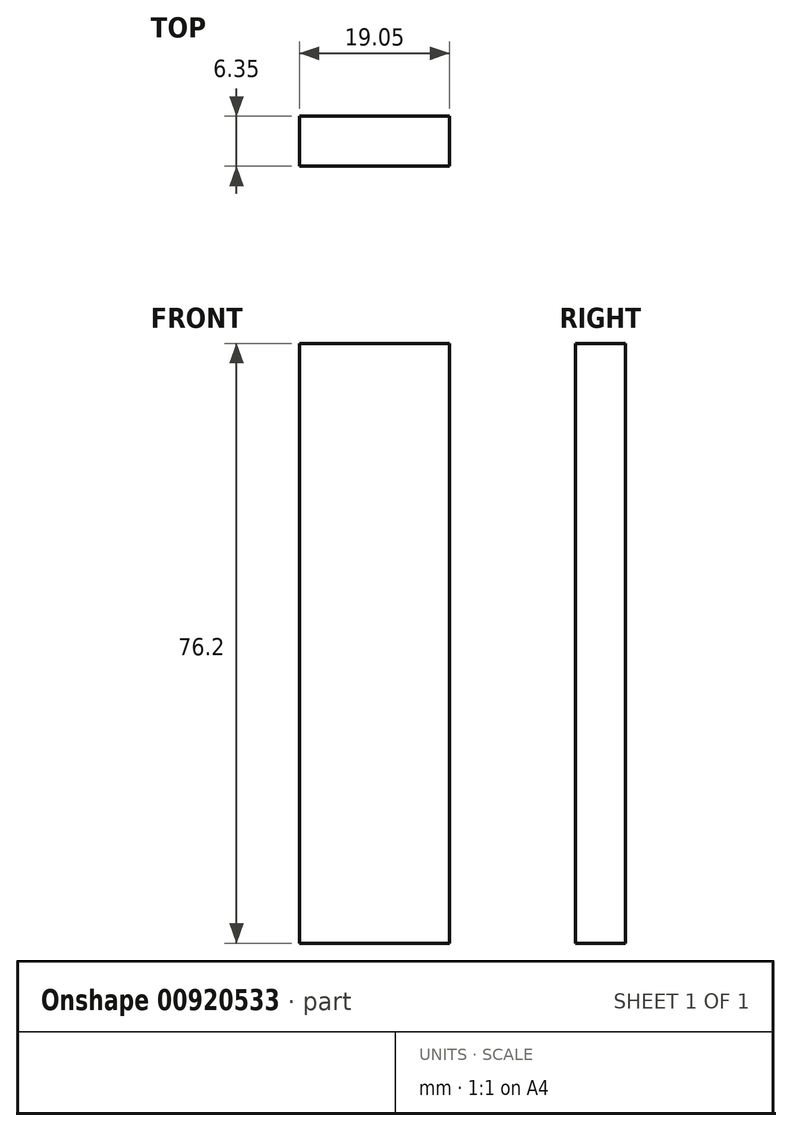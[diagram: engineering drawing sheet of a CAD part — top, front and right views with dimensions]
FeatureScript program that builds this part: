
annotation { "Feature Type Name" : "Feature", "Feature Type Description" : "" }
export const myFeature = defineFeature(function(context is Context, id is Id, definition is map)
    precondition{}
    {
        {
            var Q0;
            Q0=qCreatedBy(makeId("Front.planeOp"),FACE);
            var sketch = newSketch(context, id + "F0", { "sketchPlane" : qUnion([Q0])});
            skLineSegment(sketch, "E0.bottom", {"start": v(0, 38.1) * mm, "end": v(19.05, 38.1) * mm});
            skLineSegment(sketch, "E0.top", {"start": v(0, -38.1) * mm, "end": v(19.05, -38.1) * mm});
            skLineSegment(sketch, "E0.left", {"start": v(0, 38.1) * mm, "end": v(0, -38.1) * mm});
            skLineSegment(sketch, "E0.right", {"start": v(19.05, 38.1) * mm, "end": v(19.05, -38.1) * mm});
            skSolve(sketch);
        }
        {
            var Q0;
            Q0=makeQuery(id+"F0.imprint","IMPRINT",FACE,{"disambiguationData":[TD([[makeQuery(id+"F0.imprint","IMPRINT",EDGE,{"derivedFrom":sQuery(id+"F0.wireOp",EDGE,"E0.bottom")}),-1.0]])]});
            extrude(context, id + "F1", {"entities" : qUnion([Q0]), "oppositeDirection" : true, "depth" : 6.35 * mm, "offsetDistance" : 25.4 * mm});
        }
    });
